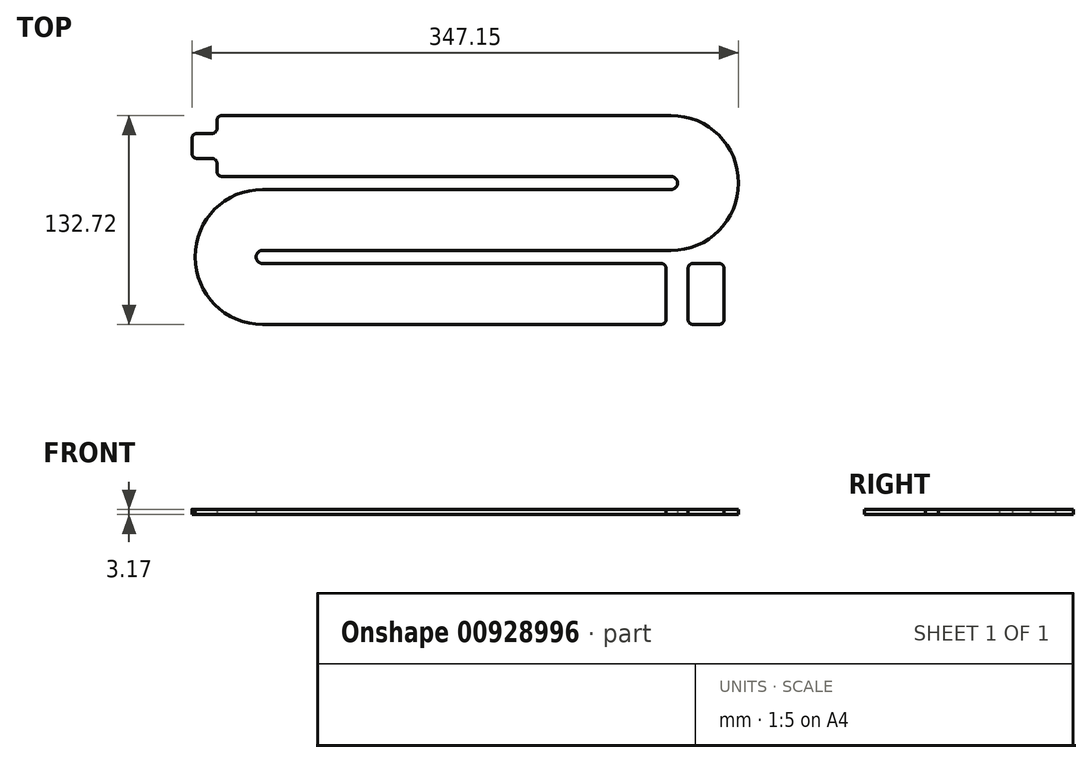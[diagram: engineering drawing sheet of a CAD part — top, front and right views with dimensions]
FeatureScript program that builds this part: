
annotation { "Feature Type Name" : "Feature", "Feature Type Description" : "" }
export const myFeature = defineFeature(function(context is Context, id is Id, definition is map)
    precondition{}
    {
        {
            var Q0;
            Q0=qCreatedBy(makeId("Top.planeOp"),FACE);
            var sketch = newSketch(context, id + "F0", { "sketchPlane" : qUnion([Q0])});
            skLineSegment(sketch, "E0.top", {"start": v(144.2, 66.36) * mm, "end": v(-144.2, 66.36) * mm});
            skPoint(sketch, "E0.middle", {"position": v(0, 0) * mm});
            skLineSegment(sketch, "E1", {"start": v(-144.2, 27.62) * mm, "end": v(144.2, 27.62) * mm});
            skArc(sketch, "E2", {"start": v(144.2, -19.37) * mm, "mid": v(187.07, 23.5) * mm, "end": v(144.2, 66.36) * mm});
            skArc(sketch, "E3", {"start": v(144.2, 19.37) * mm, "mid": v(148.34, 23.5) * mm, "end": v(144.2, 27.62) * mm});
            skLineSegment(sketch, "E4", {"start": v(-144.2, 39.05) * mm, "end": v(-160.08, 39.05) * mm});
            skLineSegment(sketch, "E5", {"start": v(-160.08, 39.05) * mm, "end": v(-160.08, 54.93) * mm});
            skLineSegment(sketch, "E6", {"start": v(-160.08, 54.93) * mm, "end": v(-144.2, 54.93) * mm});
            skLineSegment(sketch, "E7", {"start": v(-144.2, 66.36) * mm, "end": v(-144.2, 54.93) * mm});
            skLineSegment(sketch, "E8", {"start": v(-144.2, 39.05) * mm, "end": v(-144.2, 27.62) * mm});
            skLineSegment(sketch, "E9", {"start": v(-115.25, 19.37) * mm, "end": v(144.2, 19.37) * mm});
            skLineSegment(sketch, "E10", {"start": v(-115.25, -19.37) * mm, "end": v(144.2, -19.37) * mm});
            skArc(sketch, "E11", {"start": v(-115.25, 19.37) * mm, "mid": v(-158.12, -23.5) * mm, "end": v(-115.25, -66.36) * mm});
            skArc(sketch, "E12", {"start": v(-115.25, -19.37) * mm, "mid": v(-119.38, -23.5) * mm, "end": v(-115.25, -27.62) * mm});
            skLineSegment(sketch, "E13", {"start": v(141.03, -27.62) * mm, "end": v(141.03, -66.36) * mm});
            skLineSegment(sketch, "E14", {"start": v(-115.25, -27.62) * mm, "end": v(141.03, -27.62) * mm});
            skLineSegment(sketch, "E15", {"start": v(141.03, -66.36) * mm, "end": v(-115.25, -66.36) * mm});
            skLineSegment(sketch, "E16", {"start": v(155, -66.36) * mm, "end": v(155, -27.62) * mm});
            skLineSegment(sketch, "E17", {"start": v(155, -27.62) * mm, "end": v(177.86, -27.62) * mm});
            skLineSegment(sketch, "E18", {"start": v(177.86, -27.62) * mm, "end": v(177.86, -66.36) * mm});
            skLineSegment(sketch, "E19", {"start": v(177.86, -66.36) * mm, "end": v(155, -66.36) * mm});
            skSolve(sketch);
        }
        {
            var Q0;
            Q0=makeQuery(id+"F0.imprint","IMPRINT",FACE,{"disambiguationData":[TD([[makeQuery(id+"F0.imprint","IMPRINT",EDGE,{"derivedFrom":sQuery(id+"F0.wireOp",EDGE,"E0.top")}),1.0]])]});
            var Q1;
            Q1=makeQuery(id+"F0.imprint","IMPRINT",FACE,{"disambiguationData":[TD([[makeQuery(id+"F0.imprint","IMPRINT",EDGE,{"derivedFrom":sQuery(id+"F0.wireOp",EDGE,"E16")}),-1.0]])]});
            extrude(context, id + "F1", {"entities" : qUnion([Q0, Q1]), "depth" : 3.17 * mm, "offsetDistance" : 25.4 * mm});
        }
        {
            var Q0;
            Q0=makeQuery(id+"F1.opExtrude","SWEPT_EDGE",EDGE,{"disambiguationData":[OSD([sQuery(id+"F0.wireOp",EDGE,"E13"),sQuery(id+"F0.wireOp",EDGE,"E14")])]});
            var Q1;
            Q1=makeQuery(id+"F1.opExtrude","SWEPT_EDGE",EDGE,{"disambiguationData":[OSD([sQuery(id+"F0.wireOp",EDGE,"E17"),sQuery(id+"F0.wireOp",EDGE,"E18")])]});
            var Q2;
            Q2=makeQuery(id+"F1.opExtrude","SWEPT_EDGE",EDGE,{"disambiguationData":[OSD([sQuery(id+"F0.wireOp",EDGE,"E13"),sQuery(id+"F0.wireOp",EDGE,"E15")])]});
            var Q3;
            Q3=makeQuery(id+"F1.opExtrude","SWEPT_EDGE",EDGE,{"disambiguationData":[OSD([sQuery(id+"F0.wireOp",EDGE,"E16"),sQuery(id+"F0.wireOp",EDGE,"E19")])]});
            var Q4;
            Q4=makeQuery(id+"F1.opExtrude","SWEPT_EDGE",EDGE,{"disambiguationData":[OSD([sQuery(id+"F0.wireOp",EDGE,"E18"),sQuery(id+"F0.wireOp",EDGE,"E19")])]});
            var Q5;
            Q5=makeQuery(id+"F1.opExtrude","SWEPT_EDGE",EDGE,{"disambiguationData":[OSD([sQuery(id+"F0.wireOp",EDGE,"E16"),sQuery(id+"F0.wireOp",EDGE,"E17")])]});
            var Q6;
            Q6=makeQuery(id+"F1.opExtrude","SWEPT_EDGE",EDGE,{"disambiguationData":[OSD([sQuery(id+"F0.wireOp",EDGE,"E0.top"),sQuery(id+"F0.wireOp",EDGE,"E7")])]});
            var Q7;
            Q7=makeQuery(id+"F1.opExtrude","SWEPT_EDGE",EDGE,{"disambiguationData":[OSD([sQuery(id+"F0.wireOp",EDGE,"E6"),sQuery(id+"F0.wireOp",EDGE,"E7")])]});
            var Q8;
            Q8=makeQuery(id+"F1.opExtrude","SWEPT_EDGE",EDGE,{"disambiguationData":[OSD([sQuery(id+"F0.wireOp",EDGE,"E5"),sQuery(id+"F0.wireOp",EDGE,"E6")])]});
            var Q9;
            Q9=makeQuery(id+"F1.opExtrude","SWEPT_EDGE",EDGE,{"disambiguationData":[OSD([sQuery(id+"F0.wireOp",EDGE,"E4"),sQuery(id+"F0.wireOp",EDGE,"E5")])]});
            var Q10;
            Q10=makeQuery(id+"F1.opExtrude","SWEPT_EDGE",EDGE,{"disambiguationData":[OSD([sQuery(id+"F0.wireOp",EDGE,"E1"),sQuery(id+"F0.wireOp",EDGE,"E8")])]});
            var Q11;
            Q11=makeQuery(id+"F1.opExtrude","SWEPT_EDGE",EDGE,{"disambiguationData":[OSD([sQuery(id+"F0.wireOp",EDGE,"E4"),sQuery(id+"F0.wireOp",EDGE,"E8")])]});
            fillet(context, id + "F2", {"entities" : qUnion([Q0, Q1, Q2, Q3, Q4, Q5, Q6, Q7, Q8, Q9, Q10, Q11]), "radius" : 3.17 * mm, "tangentPropagation" : true, "allowEdgeOverflow" : false});
        }
    });
